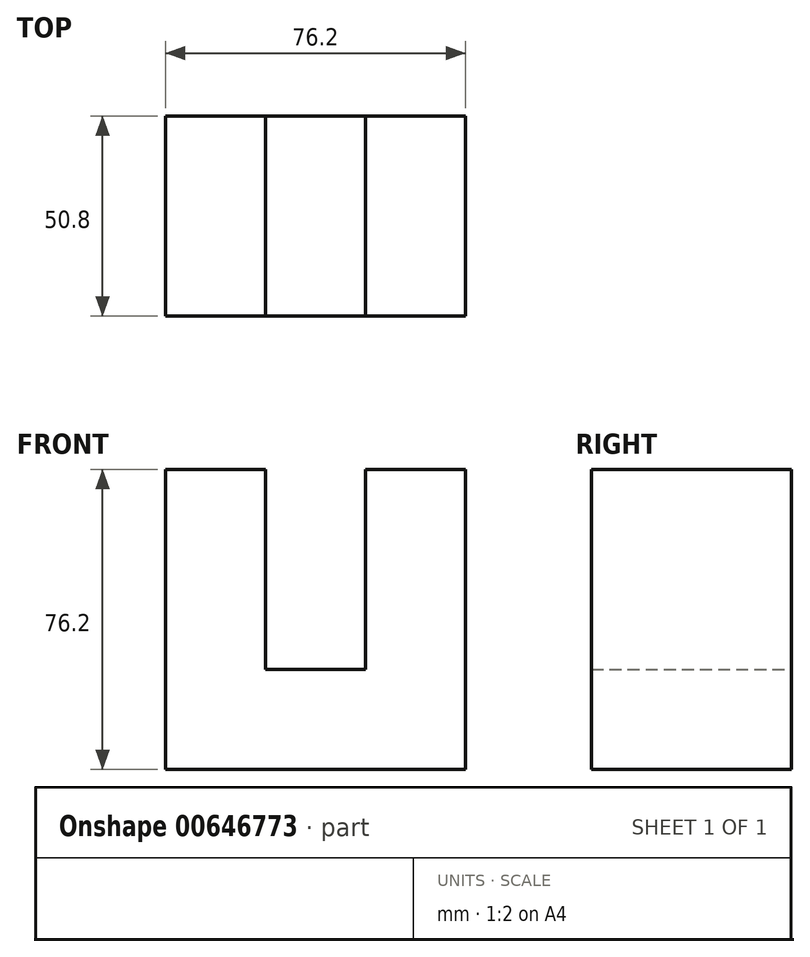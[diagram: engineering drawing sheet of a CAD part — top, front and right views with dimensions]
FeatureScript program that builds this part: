
annotation { "Feature Type Name" : "Feature", "Feature Type Description" : "" }
export const myFeature = defineFeature(function(context is Context, id is Id, definition is map)
    precondition{}
    {
        {
            var Q0;
            Q0=qCreatedBy(makeId("Front.planeOp"),FACE);
            var sketch = newSketch(context, id + "F0", { "sketchPlane" : qUnion([Q0])});
            skLineSegment(sketch, "E0", {"start": v(-21.48, 3.15) * mm, "end": v(-21.48, 53.95) * mm});
            skLineSegment(sketch, "E1", {"start": v(-21.48, 53.95) * mm, "end": v(-46.88, 53.95) * mm});
            skLineSegment(sketch, "E2", {"start": v(-46.88, 53.95) * mm, "end": v(-46.88, -22.25) * mm});
            skLineSegment(sketch, "E3", {"start": v(-46.88, -22.25) * mm, "end": v(29.32, -22.25) * mm});
            skLineSegment(sketch, "E4", {"start": v(29.32, -22.25) * mm, "end": v(29.32, 53.95) * mm});
            skLineSegment(sketch, "E5", {"start": v(29.32, 53.95) * mm, "end": v(3.92, 53.95) * mm});
            skLineSegment(sketch, "E6", {"start": v(3.92, 53.95) * mm, "end": v(3.92, 3.15) * mm});
            skLineSegment(sketch, "E7", {"start": v(3.92, 3.15) * mm, "end": v(-21.48, 3.15) * mm});
            skSolve(sketch);
        }
        {
            var Q0;
            Q0=makeQuery(id+"F0.imprint","IMPRINT",FACE,{"disambiguationData":[TD([[makeQuery(id+"F0.imprint","IMPRINT",EDGE,{"derivedFrom":sQuery(id+"F0.wireOp",EDGE,"E0")}),1.0]])]});
            extrude(context, id + "F1", {"entities" : qUnion([Q0]), "depth" : 50.8 * mm, "offsetDistance" : 25.4 * mm});
        }
    });
